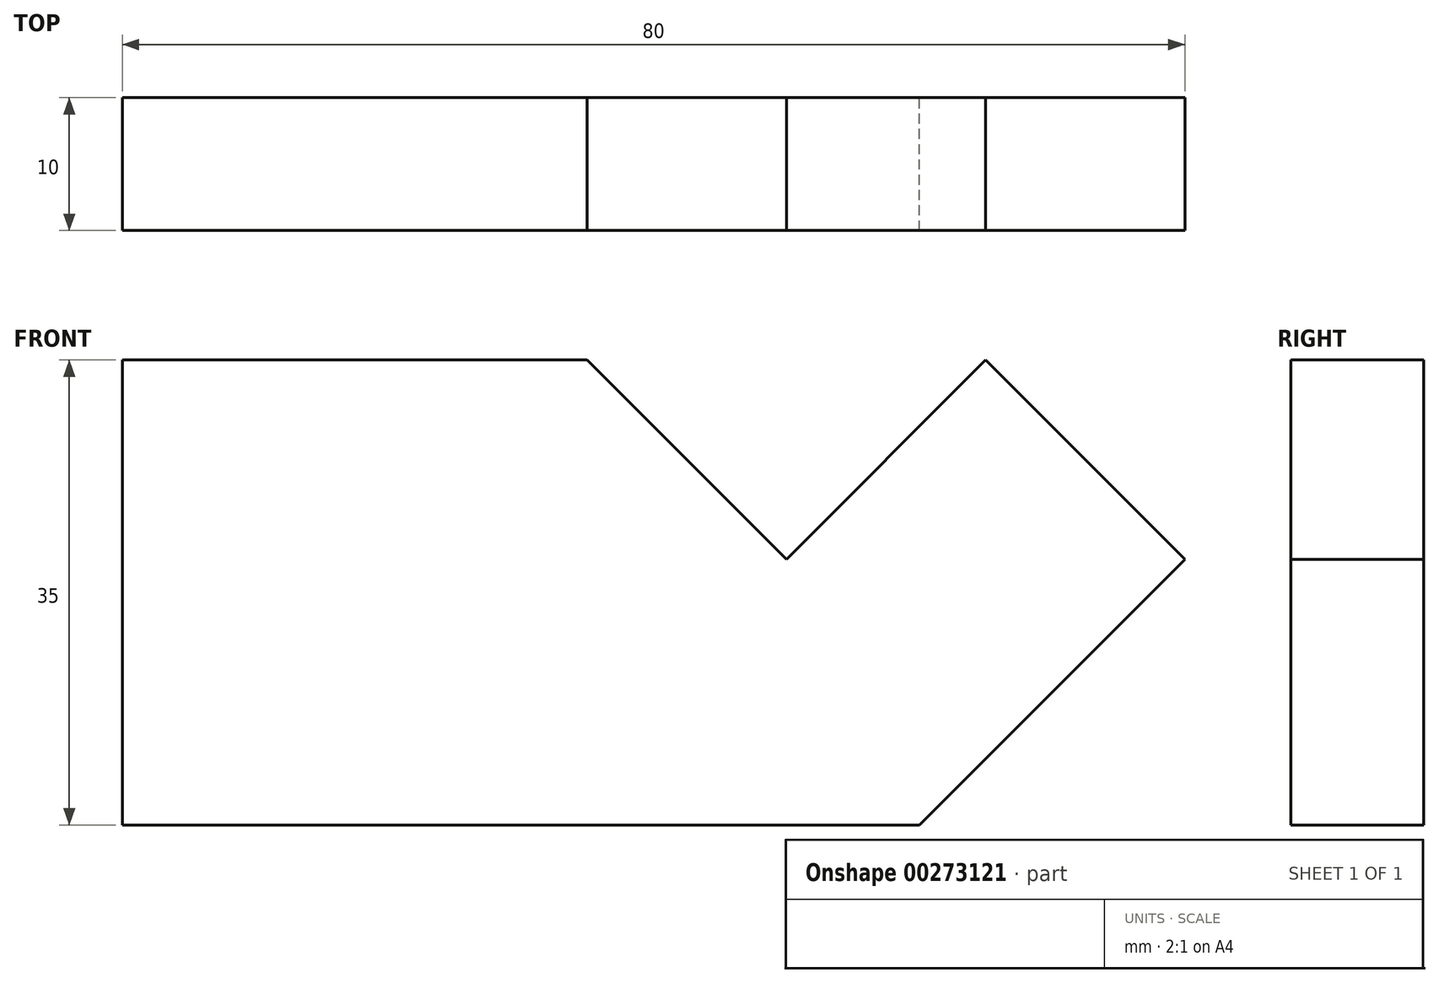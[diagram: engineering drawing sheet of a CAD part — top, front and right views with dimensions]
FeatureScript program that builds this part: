
annotation { "Feature Type Name" : "Feature", "Feature Type Description" : "" }
export const myFeature = defineFeature(function(context is Context, id is Id, definition is map)
    precondition{}
    {
        {
            var Q0;
            Q0=qCreatedBy(makeId("Front.planeOp"),FACE);
            var sketch = newSketch(context, id + "F0", { "sketchPlane" : qUnion([Q0])});
            skLineSegment(sketch, "E0", {"start": v(0, 0) * mm, "end": v(0, 35) * mm});
            skLineSegment(sketch, "E1", {"start": v(50, 20) * mm, "end": v(35, 35) * mm});
            skLineSegment(sketch, "E2", {"start": v(0, 35) * mm, "end": v(35, 35) * mm});
            skLineSegment(sketch, "E3", {"start": v(50, 20) * mm, "end": v(65, 35) * mm});
            skLineSegment(sketch, "E4", {"start": v(80, 20) * mm, "end": v(60, 0) * mm});
            skLineSegment(sketch, "E5", {"start": v(80, 20) * mm, "end": v(65, 35) * mm});
            skLineSegment(sketch, "E6", {"start": v(0, 0) * mm, "end": v(60, 0) * mm});
            skSolve(sketch);
        }
        {
            var Q0;
            Q0 = qSketchRegion(id + "F0", true);
            extrude(context, id + "F1", {"entities" : qUnion([Q0]), "depth" : 10 * mm});
        }
    });
